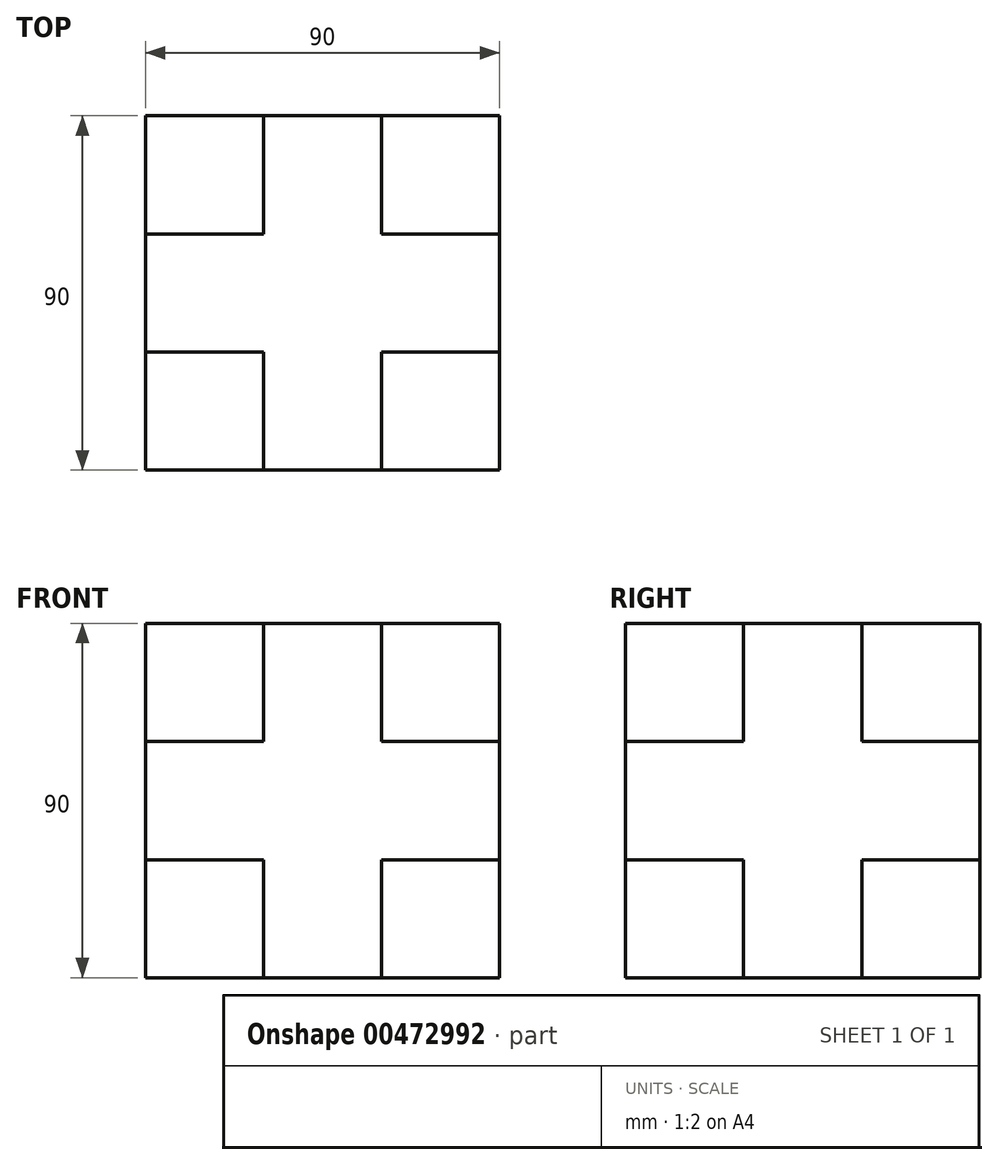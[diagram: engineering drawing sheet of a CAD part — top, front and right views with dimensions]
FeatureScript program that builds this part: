
annotation { "Feature Type Name" : "Feature", "Feature Type Description" : "" }
export const myFeature = defineFeature(function(context is Context, id is Id, definition is map)
    precondition{}
    {
        {
            var Q0;
            Q0=qCreatedBy(makeId("Top.planeOp"),FACE);
            var sketch = newSketch(context, id + "F0", { "sketchPlane" : qUnion([Q0])});
            skLineSegment(sketch, "E0.bottom", {"start": v(-45, 45) * mm, "end": v(45, 45) * mm});
            skLineSegment(sketch, "E0.top", {"start": v(-45, -45) * mm, "end": v(45, -45) * mm});
            skLineSegment(sketch, "E0.left", {"start": v(-45, 45) * mm, "end": v(-45, -45) * mm});
            skLineSegment(sketch, "E0.right", {"start": v(45, 45) * mm, "end": v(45, -45) * mm});
            skSolve(sketch);
        }
        {
            var Q0;
            Q0=makeQuery(id+"F0.imprint","IMPRINT",FACE,{"disambiguationData":[TD([[makeQuery(id+"F0.imprint","IMPRINT",EDGE,{"derivedFrom":sQuery(id+"F0.wireOp",EDGE,"E0.bottom")}),-1.0]])]});
            extrude(context, id + "F1", {"entities" : qUnion([Q0]), "depth" : 90 * mm});
        }
        {
            var Q0;
            Q0=qCreatedBy(makeId("Top.planeOp"),FACE);
            var sketch = newSketch(context, id + "F2", { "sketchPlane" : qUnion([Q0])});
            skLineSegment(sketch, "E1", {"start": v(-45.07, 45) * mm, "end": v(-15, 45) * mm});
            skLineSegment(sketch, "E2.bottom", {"start": v(-15, 45) * mm, "end": v(-45, 45) * mm});
            skLineSegment(sketch, "E2.top", {"start": v(-15, 15) * mm, "end": v(-45, 15) * mm});
            skLineSegment(sketch, "E2.left", {"start": v(-15, 45) * mm, "end": v(-15, 15) * mm});
            skLineSegment(sketch, "E2.right", {"start": v(-45, 45) * mm, "end": v(-45, 15) * mm});
            skLineSegment(sketch, "E3.MirrorCS", {"start": v(15, 45) * mm, "end": v(45, 45) * mm});
            skLineSegment(sketch, "E4.MirrorCS", {"start": v(15, 45) * mm, "end": v(15, 15) * mm});
            skLineSegment(sketch, "E5.MirrorCS", {"start": v(15, 15) * mm, "end": v(45, 15) * mm});
            skLineSegment(sketch, "E6.MirrorCS", {"start": v(45, 45) * mm, "end": v(45, 15) * mm});
            skLineSegment(sketch, "E7.MirrorCS", {"start": v(-15, -15) * mm, "end": v(-45, -15) * mm});
            skLineSegment(sketch, "E8.MirrorCS", {"start": v(-15, -45) * mm, "end": v(-15, -15) * mm});
            skLineSegment(sketch, "E9.MirrorCS", {"start": v(-45, -45) * mm, "end": v(-45, -15) * mm});
            skLineSegment(sketch, "E10.MirrorCS", {"start": v(-15, -45) * mm, "end": v(-45, -45) * mm});
            skLineSegment(sketch, "E11.MirrorCS", {"start": v(15, -15) * mm, "end": v(45, -15) * mm});
            skLineSegment(sketch, "E12.MirrorCS", {"start": v(15, -45) * mm, "end": v(15, -15) * mm});
            skLineSegment(sketch, "E13.MirrorCS", {"start": v(45, -45) * mm, "end": v(45, -15) * mm});
            skLineSegment(sketch, "E14.MirrorCS", {"start": v(15, -45) * mm, "end": v(45, -45) * mm});
            skSolve(sketch);
        }
        {
            var Q0;
            Q0=makeQuery(id+"F1.opExtrude","CAP_FACE",FACE,{"disambiguationData":[OSD([sQuery(id+"F0.wireOp",EDGE,"E0.bottom"),sQuery(id+"F0.wireOp",EDGE,"E0.top"),sQuery(id+"F0.wireOp",EDGE,"E0.left"),sQuery(id+"F0.wireOp",EDGE,"E0.right")])],"isStart":false});
            var sketch = newSketch(context, id + "F3", { "sketchPlane" : qUnion([Q0])});
            skLineSegment(sketch, "E15.bottom", {"start": v(45, 45) * mm, "end": v(15, 45) * mm});
            skLineSegment(sketch, "E15.top", {"start": v(45, 15) * mm, "end": v(15, 15) * mm});
            skLineSegment(sketch, "E15.left", {"start": v(45, 45) * mm, "end": v(45, 15) * mm});
            skLineSegment(sketch, "E15.right", {"start": v(15, 45) * mm, "end": v(15, 15) * mm});
            skLineSegment(sketch, "E16.MirrorCS", {"start": v(-15, 45) * mm, "end": v(-15, 15) * mm});
            skLineSegment(sketch, "E17.MirrorCS", {"start": v(-45, 15) * mm, "end": v(-15, 15) * mm});
            skLineSegment(sketch, "E18.MirrorCS", {"start": v(-45, -15) * mm, "end": v(-15, -15) * mm});
            skLineSegment(sketch, "E19.MirrorCS", {"start": v(-15, -45) * mm, "end": v(-15, -15) * mm});
            skLineSegment(sketch, "E20.MirrorCS", {"start": v(45, -15) * mm, "end": v(15, -15) * mm});
            skLineSegment(sketch, "E21.MirrorCS", {"start": v(15, -45) * mm, "end": v(15, -15) * mm});
            skSolve(sketch);
        }
        {
            var Q0;
            {var subQ0=sQuery(id+"F3.wireOp",EDGE,"E18.MirrorCS");Q0=makeQuery(id+"F3.imprint","IMPRINT",FACE,{"disambiguationData":[TD([[makeQuery(id+"F3.imprint","IMPRINT",EDGE,{"derivedFrom":subQ0}),-1.0]])]});}
            var Q1;
            {var subQ0=sQuery(id+"F3.wireOp",EDGE,"E16.MirrorCS");Q1=makeQuery(id+"F3.imprint","IMPRINT",FACE,{"disambiguationData":[TD([[makeQuery(id+"F3.imprint","IMPRINT",EDGE,{"derivedFrom":subQ0}),-1.0]])]});}
            var Q2;
            Q2=makeQuery(id+"F3.imprint","IMPRINT",FACE,{"disambiguationData":[TD([[makeQuery(id+"F3.imprint","IMPRINT",EDGE,{"derivedFrom":sQuery(id+"F3.wireOp",EDGE,"E15.bottom")}),-1.0]])]});
            var Q3;
            {var subQ0=sQuery(id+"F3.wireOp",EDGE,"E20.MirrorCS");Q3=makeQuery(id+"F3.imprint","IMPRINT",FACE,{"disambiguationData":[TD([[makeQuery(id+"F3.imprint","IMPRINT",EDGE,{"derivedFrom":subQ0}),1.0]])]});}
            extrude(context, id + "F4", {"entities" : qUnion([Q0, Q1, Q2, Q3]), "operationType" : NewBodyOperationType.REMOVE, "oppositeDirection" : true, "depth" : 30 * mm});
        }
        {
            var Q0;
            Q0=makeQuery(id+"F2.imprint","IMPRINT",FACE,{"disambiguationData":[TD([[makeQuery(id+"F2.imprint","IMPRINT",EDGE,{"derivedFrom":sQuery(id+"F2.wireOp",EDGE,"E3.MirrorCS")}),-1.0]])]});
            var Q1;
            Q1=makeQuery(id+"F2.imprint","IMPRINT",FACE,{"disambiguationData":[TD([[makeQuery(id+"F2.imprint","IMPRINT",EDGE,{"derivedFrom":sQuery(id+"F2.wireOp",EDGE,"E2.left")}),-1.0]])]});
            var Q2;
            Q2=makeQuery(id+"F2.imprint","IMPRINT",FACE,{"disambiguationData":[TD([[makeQuery(id+"F2.imprint","IMPRINT",EDGE,{"derivedFrom":sQuery(id+"F2.wireOp",EDGE,"E7.MirrorCS")}),1.0]])]});
            var Q3;
            Q3=makeQuery(id+"F2.imprint","IMPRINT",FACE,{"disambiguationData":[TD([[makeQuery(id+"F2.imprint","IMPRINT",EDGE,{"derivedFrom":sQuery(id+"F2.wireOp",EDGE,"E11.MirrorCS")}),-1.0]])]});
            extrude(context, id + "F5", {"entities" : qUnion([Q0, Q1, Q2, Q3]), "operationType" : NewBodyOperationType.REMOVE, "depth" : 30 * mm});
        }
    });
